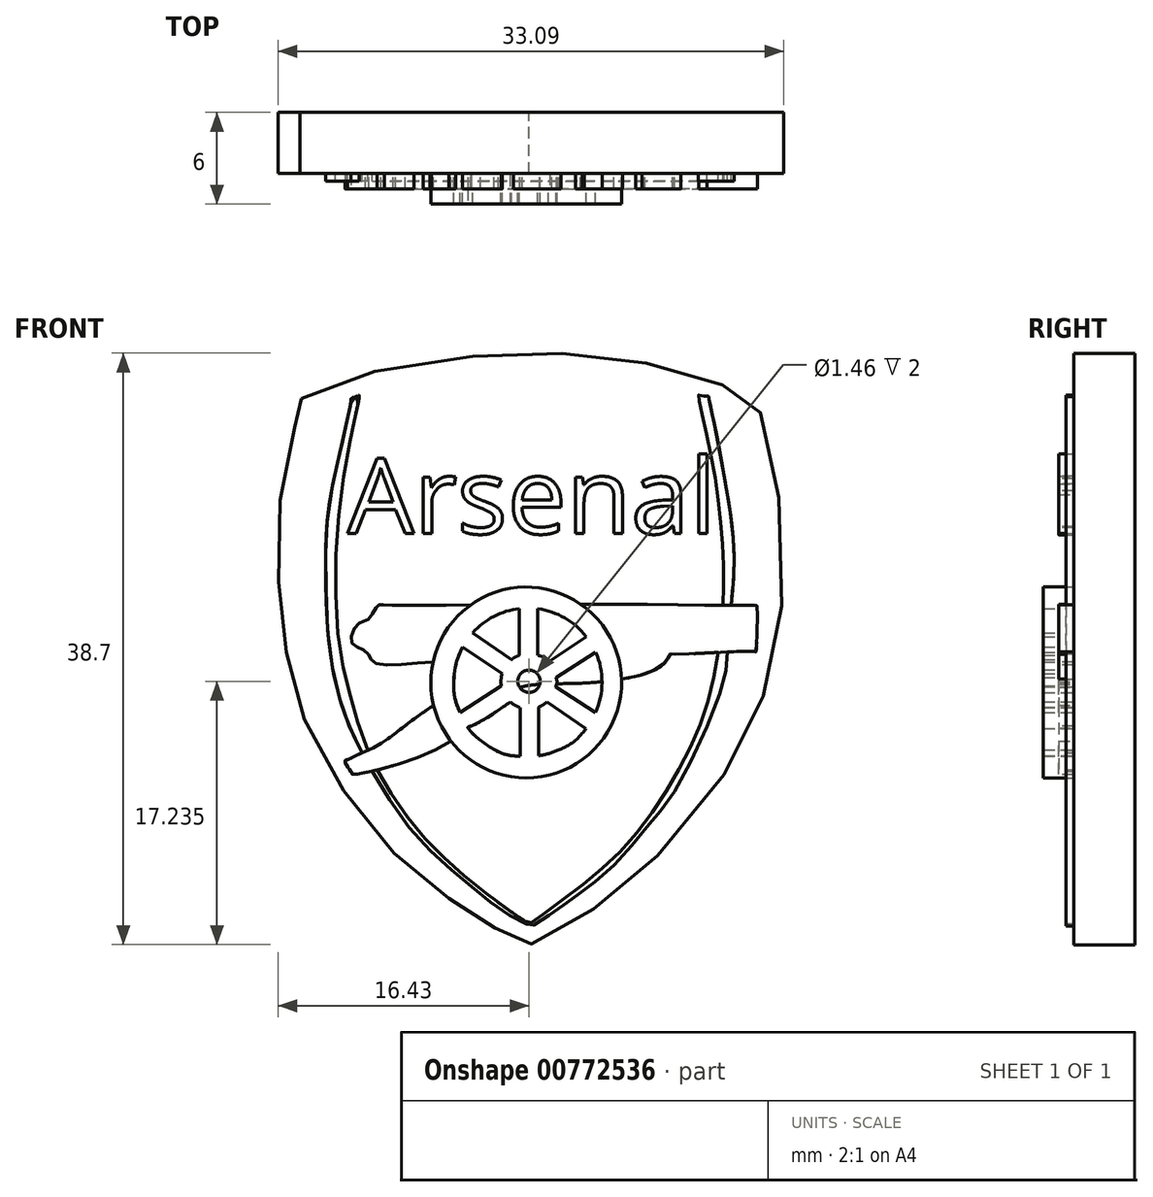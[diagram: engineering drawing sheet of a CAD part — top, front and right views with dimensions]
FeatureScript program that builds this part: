
annotation { "Feature Type Name" : "Feature", "Feature Type Description" : "" }
export const myFeature = defineFeature(function(context is Context, id is Id, definition is map)
    precondition{}
    {
        {
            var Q0;
            Q0=qCreatedBy(makeId("Front.planeOp"),FACE);
            var sketch = newSketch(context, id + "F0", { "sketchPlane" : qUnion([Q0])});
            skPoint(sketch, "E0.12.internal.snap0", {"position": v(20, 0) * mm});
            skPoint(sketch, "E0.13.internal.snap0", {"position": v(20, 0) * mm});
            skFitSpline(sketch, "E0", {"points": [v(5.13, 36.38) * mm, v(10.44, 38.27) * mm, v(18.73, 39.3) * mm, v(25.28, 39.07) * mm, v(31.25, 37.76) * mm, v(34.45, 36.38) * mm, v(35.25, 35.22) * mm, v(36.63, 27) * mm, v(35.76, 18.33) * mm, v(33.07, 12.22) * mm, v(27.1, 5.16) * mm, v(22.66, 2.04) * mm, v(20, 0.64) * mm, v(20, 0.66) * mm, v(18.14, 1.55) * mm, v(16.5, 2.5) * mm, v(13.05, 4.95) * mm, v(9.94, 7.99) * mm, v(6.24, 13.42) * mm, v(4.58, 17.65) * mm, v(3.79, 21.95) * mm, v(3.6, 26.79) * mm, v(4.19, 32.94) * mm, v(4.98, 35.32) * mm, v(5.05, 35.81) * mm, v(5.13, 36.38) * mm]});
            skSolve(sketch);
        }
        {
            var Q0;
            Q0=makeQuery(id+"F0.imprint","IMPRINT",FACE,{"disambiguationData":[TD([[makeQuery(id+"F0.imprint","IMPRINT",EDGE,{"derivedFrom":sQuery(id+"F0.wireOp",EDGE,"E0")}),-1.0]])]});
            extrude(context, id + "F1", {"entities" : qUnion([Q0]), "depth" : 4 * mm, "offsetDistance" : 25 * mm});
        }
        {
            var Q0;
            Q0=makeQuery(id+"F1.opExtrude","CAP_FACE",FACE,{"disambiguationData":[OSD([sQuery(id+"F0.wireOp",EDGE,"E0")])],"isStart":false});
            var sketch = newSketch(context, id + "F2", { "sketchPlane" : qUnion([Q0])});
            skText(sketch, "E1", { "text": "Arsenal\n", "fontName": "OpenSans-Regular.ttf"});
            skFitSpline(sketch, "E2", {"points": [v(7.96, 12.63) * mm, v(8.4, 11.87) * mm, v(8.45, 11.79) * mm, v(14.58, 13.76) * mm, v(18.73, 17.2) * mm, v(23.3, 17.74) * mm, v(28.72, 18.91) * mm, v(29.25, 19.65) * mm, v(29.44, 19.65) * mm, v(34.8, 19.81) * mm, v(34.87, 19.81) * mm, v(34.92, 22.82) * mm, v(34.8, 22.87) * mm, v(23.65, 22.92) * mm, v(10.5, 22.87) * mm, v(10.1, 22.8) * mm, v(9.45, 21.91) * mm, v(8.85, 21.66) * mm, v(8.4, 20.42) * mm, v(9.4, 19.78) * mm, v(10.03, 19.02) * mm, v(14.77, 18.95) * mm, v(14.83, 17.36) * mm, v(12.86, 15.67) * mm, v(10.12, 13.7) * mm, v(8.6, 12.97) * mm, v(8.16, 12.75) * mm, v(7.96, 12.63) * mm]});
            const initialGuessF2  = {"E1": [0.00813, 0.02753, 1, 0, 0.00496]};
            skSetInitialGuess(sketch, initialGuessF2);
            skSolve(sketch);
        }
        {
            var Q0;
            {var subQ0=sQuery(id+"F0.wireOp",EDGE,"E0");Q0=makeQuery(id+"FBtWP9GjsR8Dhei_1.boolean.opBoolean","SPLIT",FACE,{"disambiguationData":[TD([makeQuery(id+"F1.opExtrude","SWEPT_FACE",FACE,{"disambiguationData":[OSD([subQ0])]})])],"derivedFrom":makeQuery(id+"F1.opExtrude","CAP_FACE",FACE,{"disambiguationData":[OSD([subQ0])],"isStart":false})});}
            var sketch = newSketch(context, id + "F3", { "sketchPlane" : qUnion([Q0])});
            skCircle(sketch, "E3", {"center": v(19.82, 17.8) * mm, "radius": 6.24 * mm});
            skPoint(sketch, "E3.first.point", {"position": v(19.26, 24.01) * mm});
            skPoint(sketch, "E3.second.point", {"position": v(20.58, 11.6) * mm});
            skPoint(sketch, "E3.third.point", {"position": v(24.98, 14.28) * mm});
            skArc(sketch, "E4", {"start": v(19.38, 22.63) * mm, "mid": v(17.7, 22.12) * mm, "end": v(16.32, 21.05) * mm});
            skPoint(sketch, "E4.first.point", {"position": v(21.94, 13.38) * mm});
            skPoint(sketch, "E4.second.point", {"position": v(17.75, 22.14) * mm});
            skPoint(sketch, "E4.third.point", {"position": v(23, 21.57) * mm});
            skPoint(sketch, "E5.first.point", {"position": v(20.88, 19.43) * mm});
            skPoint(sketch, "E5.second.point", {"position": v(18.17, 17.84) * mm});
            skPoint(sketch, "E5.third.point", {"position": v(18.99, 16.36) * mm});
            skCircle(sketch, "E6", {"center": v(20, 17.87) * mm, "radius": 0.73 * mm});
            skPoint(sketch, "E6.first.point", {"position": v(20.04, 17.14) * mm});
            skPoint(sketch, "E6.second.point", {"position": v(19.68, 18.53) * mm});
            skPoint(sketch, "E6.third.point", {"position": v(20.7, 18.1) * mm});
            skLineSegment(sketch, "E7", {"start": v(16.32, 21.05) * mm, "end": v(18.86, 19.29) * mm});
            skLineSegment(sketch, "E8", {"start": v(15.67, 20.13) * mm, "end": v(18.24, 18.37) * mm});
            skLineSegment(sketch, "E9", {"start": v(15.48, 15.84) * mm, "end": v(18.2, 17.58) * mm});
            skLineSegment(sketch, "E10", {"start": v(19.44, 12.97) * mm, "end": v(19.44, 16.14) * mm});
            skLineSegment(sketch, "E11", {"start": v(20.63, 16.18) * mm, "end": v(20.63, 13) * mm});
            skLineSegment(sketch, "E12", {"start": v(21.19, 16.53) * mm, "end": v(23.74, 14.78) * mm});
            skLineSegment(sketch, "E13", {"start": v(21.75, 17.52) * mm, "end": v(24.37, 15.82) * mm});
            skLineSegment(sketch, "E14", {"start": v(21.77, 18.1) * mm, "end": v(24.37, 19.78) * mm});
            skLineSegment(sketch, "E15", {"start": v(21.28, 19.13) * mm, "end": v(23.76, 20.8) * mm});
            skLineSegment(sketch, "E16", {"start": v(20.58, 19.57) * mm, "end": v(20.58, 22.62) * mm});
            skLineSegment(sketch, "E17", {"start": v(19.38, 19.57) * mm, "end": v(19.38, 22.63) * mm});
            skArc(sketch, "E18.trimOffspring", {"start": v(24.37, 15.82) * mm, "mid": v(24.79, 17.8) * mm, "end": v(24.37, 19.78) * mm});
            skArc(sketch, "E19.trimOffspring", {"start": v(20.63, 13) * mm, "mid": v(21.3, 13.14) * mm, "end": v(21.94, 13.38) * mm});
            skArc(sketch, "E20.trimOffspring", {"start": v(23.76, 20.8) * mm, "mid": v(22.35, 22.02) * mm, "end": v(20.58, 22.62) * mm});
            skArc(sketch, "E21.trimOffspring", {"start": v(20.63, 16.18) * mm, "mid": v(20.92, 16.33) * mm, "end": v(21.19, 16.53) * mm});
            skArc(sketch, "E22.trimOffspring", {"start": v(18.24, 18.37) * mm, "mid": v(18.18, 17.98) * mm, "end": v(18.2, 17.58) * mm});
            skArc(sketch, "E23.trimOffspring", {"start": v(18.79, 16.51) * mm, "mid": v(19.1, 16.3) * mm, "end": v(19.44, 16.14) * mm});
            skFitSpline(sketch, "E24", {"points": [v(15.67, 20.13) * mm, v(15.23, 18.98) * mm, v(15.12, 16.98) * mm, v(15.48, 15.84) * mm], "startDerivative": vector(-1.6, -3.33) * mm, "endDerivative": vector(1.47, -3.34) * mm});
            skFitSpline(sketch, "E25", {"points": [v(21.94, 13.38) * mm, v(22.95, 13.92) * mm, v(23.74, 14.78) * mm], "startDerivative": vector(2.14, 0.94) * mm, "endDerivative": vector(1.45, 1.87) * mm});
            skFitSpline(sketch, "E26", {"points": [v(21.75, 17.52) * mm, v(21.84, 17.84) * mm, v(21.77, 18.1) * mm], "startDerivative": vector(0.25, 0.63) * mm, "endDerivative": vector(-0.22, 0.55) * mm});
            skFitSpline(sketch, "E27", {"points": [v(18.86, 19.29) * mm, v(19.04, 19.42) * mm, v(19.38, 19.57) * mm], "startDerivative": vector(0.37, 0.32) * mm, "endDerivative": vector(0.66, 0.26) * mm});
            skFitSpline(sketch, "E28", {"points": [v(20.58, 19.57) * mm, v(20.97, 19.43) * mm, v(21.28, 19.13) * mm], "startDerivative": vector(0.83, -0.2) * mm, "endDerivative": vector(0.56, -0.68) * mm});
            skFitSpline(sketch, "E29", {"points": [v(18.79, 16.51) * mm, v(16.25, 14.96) * mm, v(16, 14.84) * mm, v(17.83, 13.35) * mm, v(19.44, 12.97) * mm], "startDerivative": vector(-9, -6.14) * mm, "endDerivative": vector(5.67, -0.22) * mm});
            skSolve(sketch);
        }
        {
            var Q0;
            Q0=makeQuery(id+"F3.imprint","IMPRINT",FACE,{"disambiguationData":[TD([[makeQuery(id+"F3.imprint","IMPRINT",EDGE,{"derivedFrom":sQuery(id+"F3.wireOp",EDGE,"E3")}),1.0]])]});
            extrude(context, id + "F4", {"entities" : qUnion([Q0]), "operationType" : NewBodyOperationType.ADD, "depth" : 2 * mm, "offsetDistance" : 25 * mm});
        }
        {
            var Q0;
            Q0 = qSketchRegion(id + "F2", true);
            extrude(context, id + "F5", {"entities" : qUnion([Q0]), "operationType" : NewBodyOperationType.ADD, "depth" : 1 * mm, "offsetDistance" : 25 * mm});
        }
        {
            var Q0;
            Q0=makeQuery(id+"F2.imprint","IMPRINT",FACE,{"disambiguationData":[TD([[makeQuery(id+"F2.imprint","IMPRINT",EDGE,{"derivedFrom":sQuery(id+"F2.wireOp",EDGE,"E1.sketch_text.stroke-0")}),1.0]])]});
            var sketch = newSketch(context, id + "F6", { "sketchPlane" : qUnion([Q0])});
            skFitSpline(sketch, "E30", {"points": [v(8.35, 36.26) * mm, v(7.07, 30.22) * mm, v(6.7, 26.05) * mm, v(6.93, 20.24) * mm, v(7.8, 16.17) * mm, v(9.08, 13.2) * mm, v(12.46, 7.96) * mm, v(15.94, 4.7) * mm, v(18.6, 2.65) * mm, v(20.08, 1.88) * mm, v(20.2, 1.87) * mm, v(21.64, 2.77) * mm, v(22.96, 3.73) * mm, v(25.4, 5.67) * mm, v(27.8, 8.42) * mm, v(29.58, 10.77) * mm, v(32.61, 17.42) * mm, v(33.01, 19.85) * mm, v(33.3, 23.5) * mm, v(33.26, 28.26) * mm, v(31.74, 36.54) * mm, v(31.73, 36.52) * mm, v(31.15, 36.6) * mm, v(31.1, 36.58) * mm, v(31.8, 33.24) * mm, v(32.71, 26.08) * mm, v(32.48, 20.45) * mm, v(31.43, 15.7) * mm, v(29.4, 11.37) * mm, v(26.45, 7.23) * mm, v(22.8, 4.03) * mm, v(20.16, 2.08) * mm, v(20, 2.05) * mm, v(16.84, 4.27) * mm, v(12.7, 8.2) * mm, v(9.54, 13.15) * mm, v(8.52, 16.22) * mm, v(7.7, 19.44) * mm, v(7.35, 24.9) * mm, v(7.81, 30.85) * mm, v(8.52, 34.58) * mm, v(8.69, 35.43) * mm, v(8.9, 36.58) * mm, v(8.86, 36.58) * mm, v(8.37, 36.41) * mm, v(8.35, 36.26) * mm]});
            skSolve(sketch);
        }
        {
            var Q0;
            Q0 = qSketchRegion(id + "F6", true);
            extrude(context, id + "F7", {"entities" : qUnion([Q0]), "operationType" : NewBodyOperationType.ADD, "depth" : 0.5 * mm, "offsetDistance" : 25 * mm});
        }
    });
